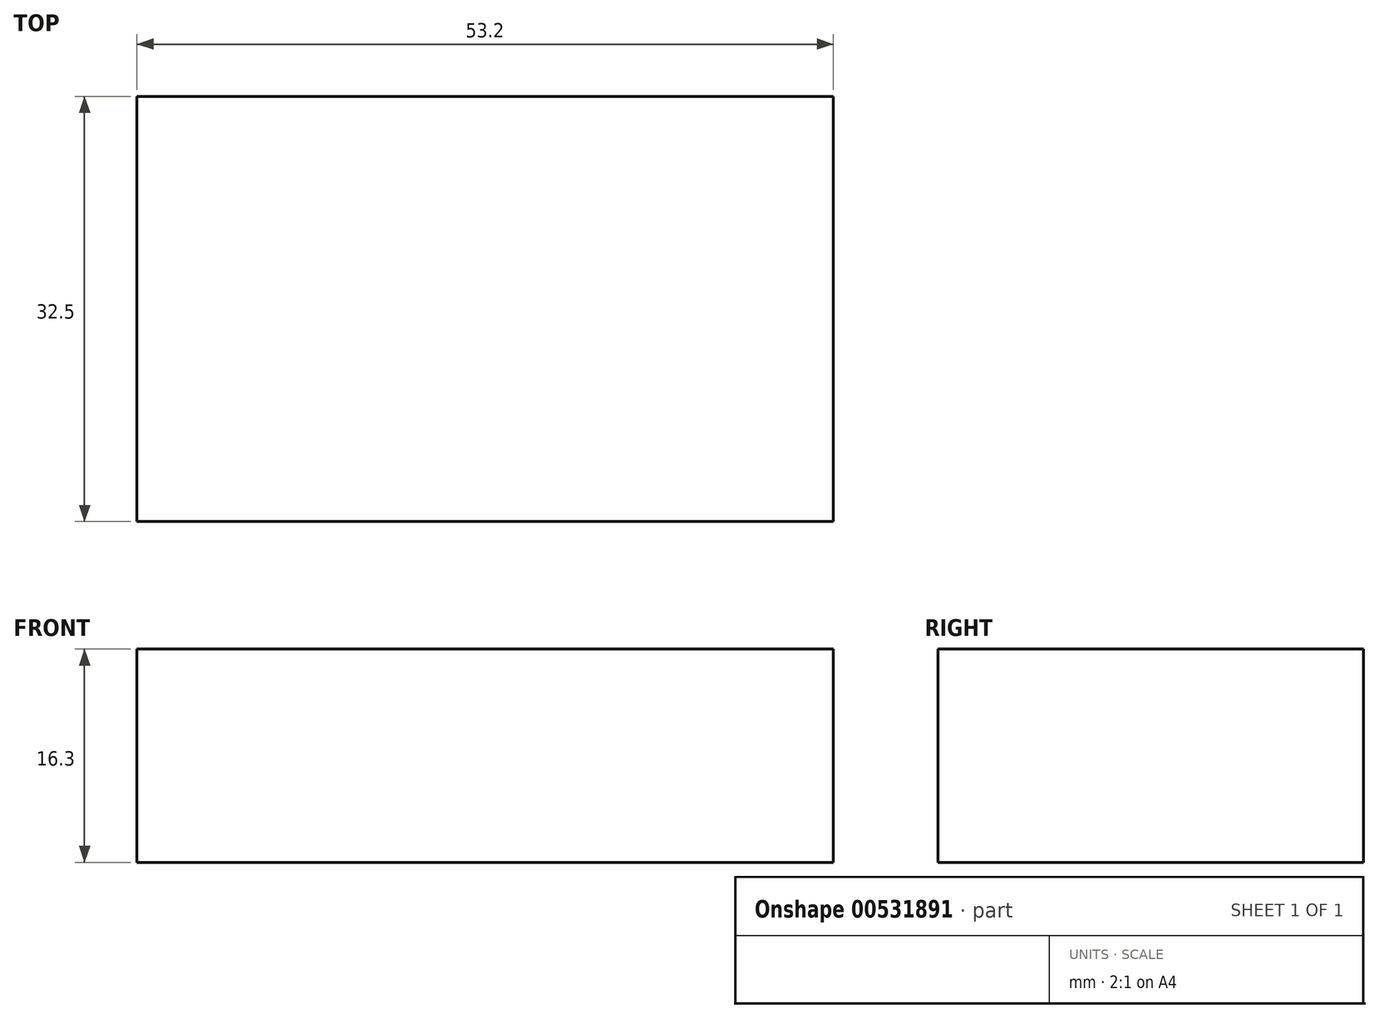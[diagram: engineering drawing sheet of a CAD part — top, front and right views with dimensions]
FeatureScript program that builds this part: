
annotation { "Feature Type Name" : "Feature", "Feature Type Description" : "" }
export const myFeature = defineFeature(function(context is Context, id is Id, definition is map)
    precondition{}
    {
        {
            var Q0;
            Q0=qCreatedBy(makeId("Front.planeOp"),FACE);
            var sketch = newSketch(context, id + "F0", { "sketchPlane" : qUnion([Q0])});
            skLineSegment(sketch, "E0.bottom", {"start": v(26.6, 8.15) * mm, "end": v(-26.6, 8.15) * mm});
            skLineSegment(sketch, "E0.top", {"start": v(26.6, -8.15) * mm, "end": v(-26.6, -8.15) * mm});
            skLineSegment(sketch, "E0.left", {"start": v(26.6, 8.15) * mm, "end": v(26.6, -8.15) * mm});
            skLineSegment(sketch, "E0.right", {"start": v(-26.6, 8.15) * mm, "end": v(-26.6, -8.15) * mm});
            skPoint(sketch, "E0.middle", {"position": v(0, 0) * mm});
            skSolve(sketch);
        }
        {
            var Q0;
            Q0 = qSketchRegion(id + "F0", true);
            extrude(context, id + "F1", {"entities" : qUnion([Q0]), "depth" : 32.5 * mm, "offsetDistance" : 25 * mm});
        }
    });
